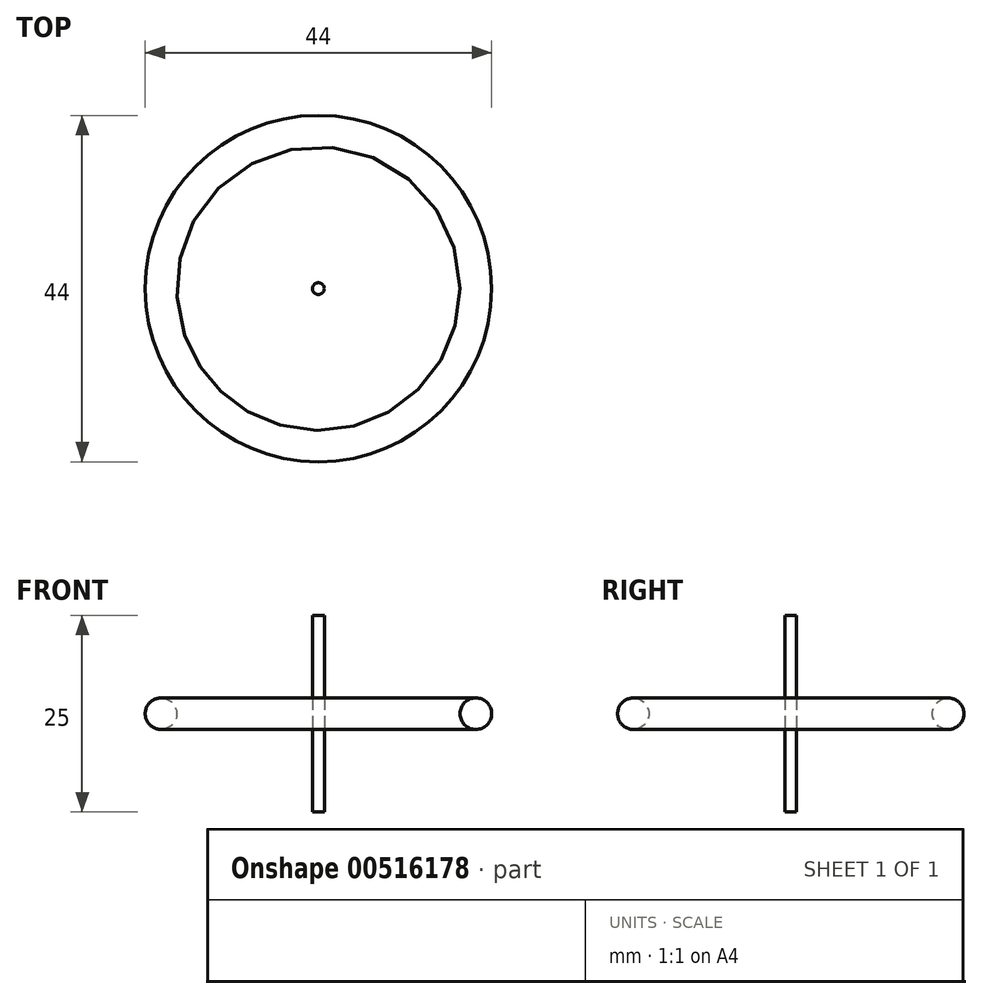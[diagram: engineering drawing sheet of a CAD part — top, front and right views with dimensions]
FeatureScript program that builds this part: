
annotation { "Feature Type Name" : "Feature", "Feature Type Description" : "" }
export const myFeature = defineFeature(function(context is Context, id is Id, definition is map)
    precondition{}
    {
        {
            var Q0;
            Q0=qCreatedBy(makeId("Front.planeOp"),FACE);
            var sketch = newSketch(context, id + "F0", { "sketchPlane" : qUnion([Q0])});
            skLineSegment(sketch, "E0", {"start": v(0, 0) * mm, "end": v(20, 0) * mm, "construction": true});
            skCircle(sketch, "E1", {"center": v(20, 0) * mm, "radius": 2 * mm});
            skLineSegment(sketch, "E2", {"start": v(0, 0) * mm, "end": v(0, -25.2) * mm, "construction": true});
            skSolve(sketch);
        }
        {
            var Q0;
            Q0=makeQuery(id+"F0.imprint","IMPRINT",FACE,{"disambiguationData":[TD([[makeQuery(id+"F0.imprint","IMPRINT",EDGE,{"derivedFrom":sQuery(id+"F0.wireOp",EDGE,"E1")}),1.0]])]});
            var Q1;
            Q1=sQuery(id+"F0.wireOp",EDGE,"E2");
            revolve(context, id + "F1", {"entities" : qUnion([Q0]), "axis" : qUnion([Q1]), "revolveType" : RevolveType.FULL});
        }
        {
            var Q0;
            Q0=qCreatedBy(makeId("Top.planeOp"),FACE);
            var sketch = newSketch(context, id + "F2", { "sketchPlane" : qUnion([Q0])});
            skCircle(sketch, "E3", {"center": v(0, 0) * mm, "radius": 0.75 * mm});
            skSolve(sketch);
        }
        {
            var Q0;
            Q0 = qSketchRegion(id + "F2", true);
            extrude(context, id + "F3", {"entities" : qUnion([Q0]), "endBound" : BoundingType.SYMMETRIC, "depth" : 25 * mm, "offsetDistance" : 25 * mm});
        }
    });
